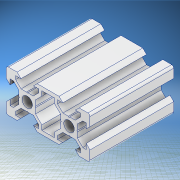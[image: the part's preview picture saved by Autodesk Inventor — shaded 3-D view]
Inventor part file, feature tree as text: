
AUTODESK INVENTOR PART (.ipt)
format: ipt  version: 2020.2 (Build 242310000, 310)  size: 256,512 bytes
history: native  units: mm
features: extrude x1, sketch x1
ambient origin geometry x8: Origin, YZ Plane, XZ Plane, XY Plane, X Axis, Y Axis, Z Axis, Center Point
bodies: Solid1 (feature_tree)
feature tree (2):
  extrude  "Extrusion1"  Depth=40.0mm TaperAngle=0.0deg
  sketch  "Sketch1"  dims[d1=40.0mm d2=360.0deg d3=40.0mm d4=0.0mm d7=1.5mm]
